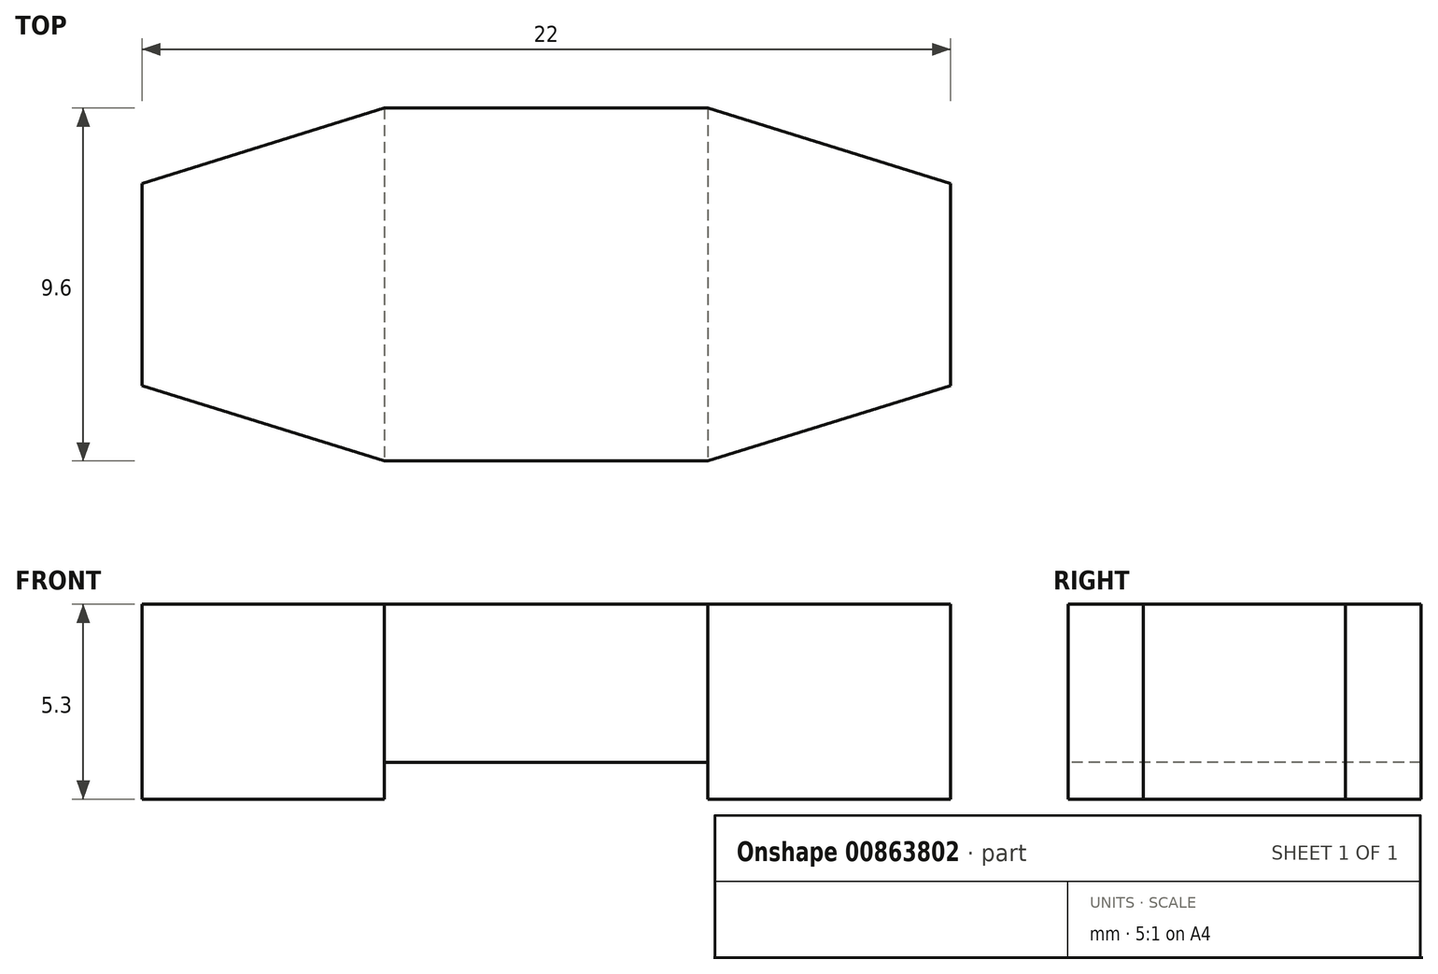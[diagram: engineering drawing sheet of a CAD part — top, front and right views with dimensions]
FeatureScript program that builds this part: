
annotation { "Feature Type Name" : "Feature", "Feature Type Description" : "" }
export const myFeature = defineFeature(function(context is Context, id is Id, definition is map)
    precondition{}
    {
        {
            var Q0;
            Q0=qCreatedBy(makeId("Top.planeOp"),FACE);
            var sketch = newSketch(context, id + "F0", { "sketchPlane" : qUnion([Q0])});
            skLineSegment(sketch, "E0.bottom", {"start": v(0, 0) * mm, "end": v(6.6, -2.05) * mm});
            skLineSegment(sketch, "E0.top", {"start": v(0, 5.5) * mm, "end": v(6.6, 7.55) * mm});
            skLineSegment(sketch, "E0.left", {"start": v(0, 0) * mm, "end": v(0, 5.5) * mm});
            skLineSegment(sketch, "E0.right", {"start": v(22, 0) * mm, "end": v(22, 5.5) * mm});
            skLineSegment(sketch, "E1", {"start": v(15.4, 7.55) * mm, "end": v(22, 5.5) * mm});
            skLineSegment(sketch, "E2", {"start": v(15.4, -2.05) * mm, "end": v(22, 0) * mm});
            skLineSegment(sketch, "E3", {"start": v(15.4, -2.05) * mm, "end": v(6.6, -2.05) * mm});
            skLineSegment(sketch, "E4", {"start": v(15.4, 7.55) * mm, "end": v(6.6, 7.55) * mm});
            skSolve(sketch);
        }
        {
            var Q0;
            Q0 = qSketchRegion(id + "F0", true);
            extrude(context, id + "F1", {"entities" : qUnion([Q0]), "depth" : 5.3 * mm, "offsetDistance" : 25 * mm});
        }
        {
            var Q0;
            Q0=makeQuery(id+"F1.opExtrude","CAP_FACE",FACE,{"disambiguationData":[OSD([sQuery(id+"F0.wireOp",EDGE,"E0.bottom"),sQuery(id+"F0.wireOp",EDGE,"E0.top"),sQuery(id+"F0.wireOp",EDGE,"E0.left"),sQuery(id+"F0.wireOp",EDGE,"E0.right")])],"isStart":true});
            var sketch = newSketch(context, id + "F2", { "sketchPlane" : qUnion([Q0])});
            skLineSegment(sketch, "E5.bottom", {"start": v(15.4, -7.55) * mm, "end": v(6.6, -7.55) * mm});
            skLineSegment(sketch, "E5.top", {"start": v(15.4, 2.05) * mm, "end": v(6.6, 2.05) * mm});
            skLineSegment(sketch, "E5.left", {"start": v(15.4, -7.55) * mm, "end": v(15.4, 2.05) * mm});
            skLineSegment(sketch, "E5.right", {"start": v(6.6, -7.55) * mm, "end": v(6.6, 2.05) * mm});
            skLineSegment(sketch, "E6", {"start": v(0, -2.75) * mm, "end": v(22, -2.75) * mm, "construction": true});
            skPoint(sketch, "E7", {"position": v(11, -2.75) * mm});
            skSolve(sketch);
        }
        {
            var Q0;
            Q0 = qSketchRegion(id + "F2", true);
            extrude(context, id + "F3", {"entities" : qUnion([Q0]), "operationType" : NewBodyOperationType.REMOVE, "oppositeDirection" : true, "depth" : 1 * mm, "offsetDistance" : 25 * mm});
        }
    });
